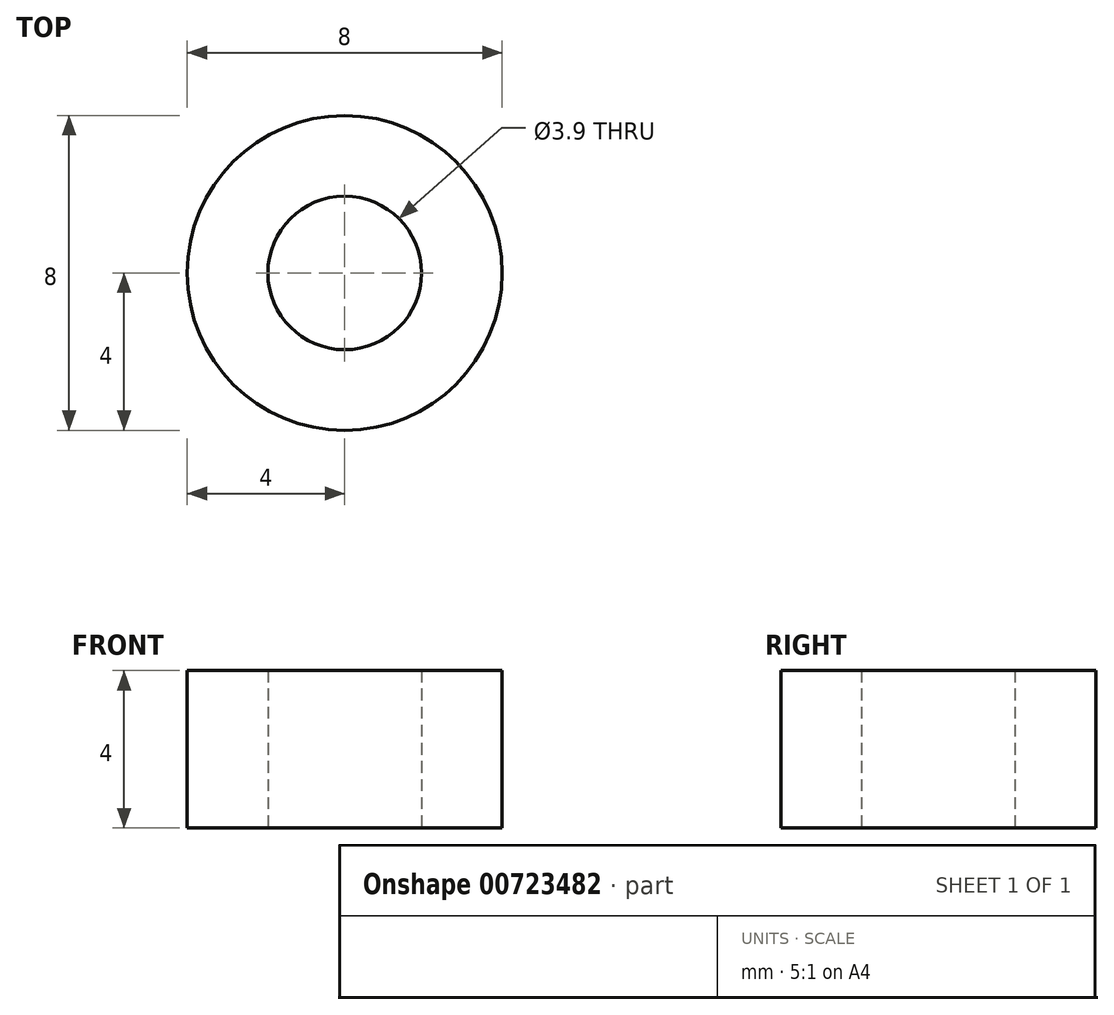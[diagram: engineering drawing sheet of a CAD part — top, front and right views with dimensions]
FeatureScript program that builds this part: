
annotation { "Feature Type Name" : "Feature", "Feature Type Description" : "" }
export const myFeature = defineFeature(function(context is Context, id is Id, definition is map)
    precondition{}
    {
        {
            var Q0;
            Q0=qCreatedBy(makeId("Top.planeOp"),FACE);
            var sketch = newSketch(context, id + "F0", { "sketchPlane" : qUnion([Q0])});
            skCircle(sketch, "E0", {"center": v(0, 0) * mm, "radius": 1.95 * mm});
            skCircle(sketch, "E1", {"center": v(0, 0) * mm, "radius": 4 * mm});
            skSolve(sketch);
        }
        {
            var Q0;
            Q0 = qSketchRegion(id + "F0", true);
            extrude(context, id + "F1", {"entities" : qUnion([Q0]), "depth" : 4 * mm, "offsetDistance" : 25 * mm});
        }
    });
